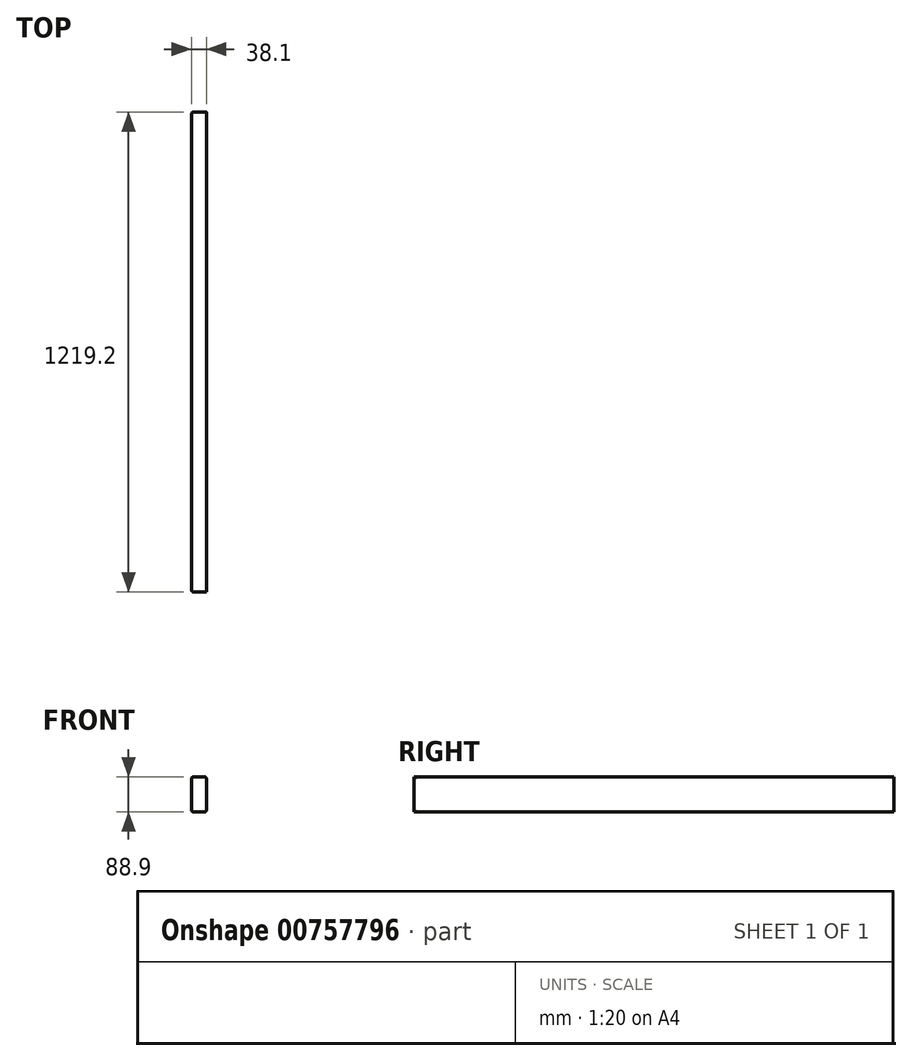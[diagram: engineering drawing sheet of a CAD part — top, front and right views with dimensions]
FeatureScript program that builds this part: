
annotation { "Feature Type Name" : "Feature", "Feature Type Description" : "" }
export const myFeature = defineFeature(function(context is Context, id is Id, definition is map)
    precondition{}
    {
        {
            var Q0;
            Q0=qCreatedBy(makeId("Front.planeOp"),FACE);
            var sketch = newSketch(context, id + "F0", { "sketchPlane" : qUnion([Q0])});
            skLineSegment(sketch, "E0.bottom", {"start": v(-18.62, 54.1) * mm, "end": v(19.48, 54.1) * mm});
            skLineSegment(sketch, "E0.top", {"start": v(-18.62, -34.8) * mm, "end": v(19.48, -34.8) * mm});
            skLineSegment(sketch, "E0.left", {"start": v(-18.62, 54.1) * mm, "end": v(-18.62, -34.8) * mm});
            skLineSegment(sketch, "E0.right", {"start": v(19.48, 54.1) * mm, "end": v(19.48, -34.8) * mm});
            skSolve(sketch);
        }
        {
            var Q0;
            Q0=makeQuery(id+"F0.imprint","IMPRINT",FACE,{"disambiguationData":[TD([[makeQuery(id+"F0.imprint","IMPRINT",EDGE,{"derivedFrom":sQuery(id+"F0.wireOp",EDGE,"E0.bottom")}),-1.0]])]});
            extrude(context, id + "F1", {"entities" : qUnion([Q0]), "depth" : 1219.2 * mm, "offsetDistance" : 25.4 * mm});
        }
        {
            var Q0;
            Q0=makeQuery(id+"F1.opExtrude","SWEPT_EDGE",EDGE,{"disambiguationData":[OSD([sQuery(id+"F0.wireOp",EDGE,"E0.bottom"),sQuery(id+"F0.wireOp",EDGE,"E0.left")])]});
            var Q1;
            Q1=makeQuery(id+"F1.opExtrude","SWEPT_EDGE",EDGE,{"disambiguationData":[OSD([sQuery(id+"F0.wireOp",EDGE,"E0.bottom"),sQuery(id+"F0.wireOp",EDGE,"E0.right")])]});
            var Q2;
            Q2=makeQuery(id+"F1.opExtrude","SWEPT_FACE",FACE,{"disambiguationData":[OSD([sQuery(id+"F0.wireOp",EDGE,"E0.left")])]});
            var Q3;
            Q3=makeQuery(id+"F1.opExtrude","SWEPT_EDGE",EDGE,{"disambiguationData":[OSD([sQuery(id+"F0.wireOp",EDGE,"E0.top"),sQuery(id+"F0.wireOp",EDGE,"E0.right")])]});
            fillet(context, id + "F2", {"entities" : qUnion([Q0, Q1, Q2, Q3]), "radius" : 5.08 * mm, "tangentPropagation" : true, "allowEdgeOverflow" : false});
        }
    });
